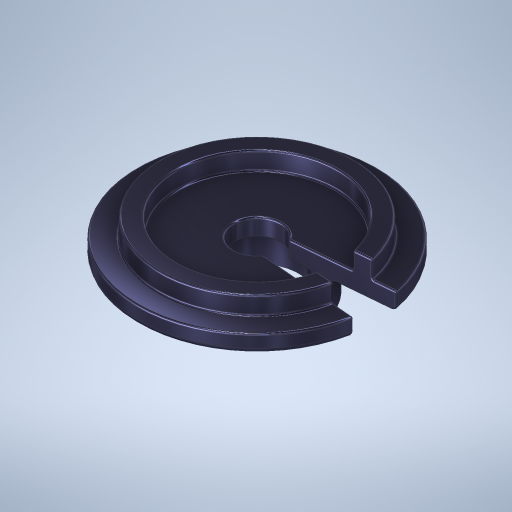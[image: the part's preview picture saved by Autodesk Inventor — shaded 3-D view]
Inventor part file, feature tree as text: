
AUTODESK INVENTOR PART (.ipt)
format: ipt  version: 2023.1 (Build 271208000, 208)  size: 528,384 bytes
history: native  units: in
note: dims shown in document units (in); Inventor stores cm internally (conversion verified against a paired STEP export)
features: fillet x3, sketch x2, revolve x1, extrude x1, projected_geometry x1
ambient origin geometry x8: Origin, YZ Plane, XZ Plane, XY Plane, X Axis, Y Axis, Z Axis, Center Point
bodies: Solid1 (feature_tree)
feature tree (8):
  revolve  "Revolution1"  [1 undecoded]
  fillet  "Fillet1"  Radius=0.45in
  extrude  "Extrusion1"  Depth=0.005in
  fillet  "Fillet2"  Radius=0.05in
  fillet  "Fillet3"  Radius=0.675in
  sketch  "Sketch1"  dims[d0=0.13in d1=0.05in d2=0.45in]
  sketch  "Sketch2"  dims[d3=0.05in d4=0.1in d5=0.05in d6=0.675in d7=0.235in d8=90.0deg d9=0.015in d10=0.0625in d11=0.0687in d12=0.0in d13=0.0in d14=0.005in d15=0.005in]
  projected_geometry  "Project Cut Edges1"
note: 1 required parameter value undecoded (feature->parameter linkage not recoverable at this tier; creation-order binding heuristic only, values carry confidence <= 0.55)
